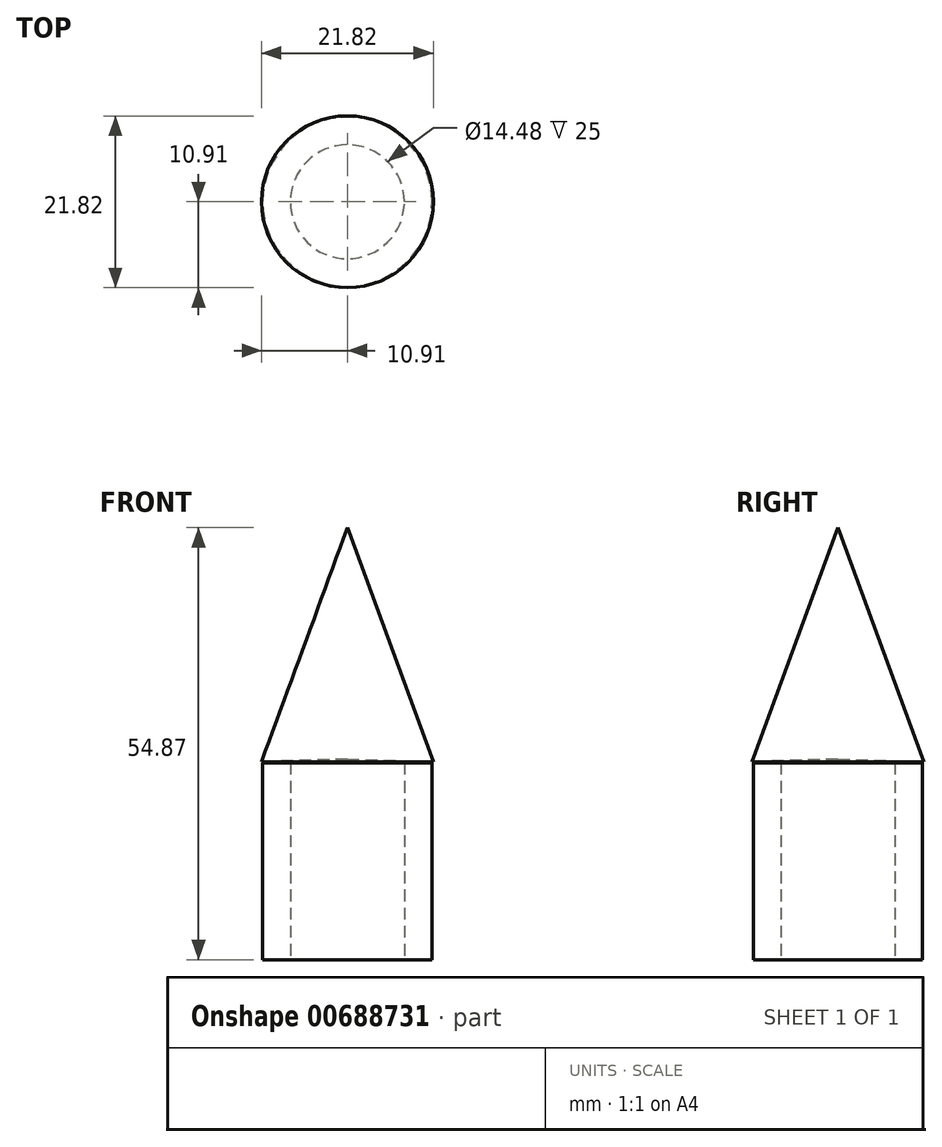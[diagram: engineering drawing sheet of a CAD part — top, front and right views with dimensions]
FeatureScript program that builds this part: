
annotation { "Feature Type Name" : "Feature", "Feature Type Description" : "" }
export const myFeature = defineFeature(function(context is Context, id is Id, definition is map)
    precondition{}
    {
        {
            var Q0;
            Q0=qCreatedBy(makeId("Top.planeOp"),FACE);
            var sketch = newSketch(context, id + "F0", { "sketchPlane" : qUnion([Q0])});
            skCircle(sketch, "E0", {"center": v(0, 0) * mm, "radius": 10.75 * mm});
            skCircle(sketch, "E1", {"center": v(0, 0) * mm, "radius": 7.24 * mm});
            skSolve(sketch);
        }
        {
            var Q0;
            Q0=makeQuery(id+"F0.imprint","IMPRINT",FACE,{"disambiguationData":[TD([[makeQuery(id+"F0.imprint","IMPRINT",EDGE,{"derivedFrom":sQuery(id+"F0.wireOp",EDGE,"E0")}),1.0]])]});
            extrude(context, id + "F1", {"entities" : qUnion([Q0]), "depth" : 25 * mm, "offsetDistance" : 25 * mm});
        }
        {
            var Q0;
            Q0=qCreatedBy(makeId("Right.planeOp"),FACE);
            var sketch = newSketch(context, id + "F2", { "sketchPlane" : qUnion([Q0])});
            skLineSegment(sketch, "E2", {"start": v(0, 25.46) * mm, "end": v(0, 54.87) * mm});
            skLineSegment(sketch, "E3", {"start": v(0, 54.87) * mm, "end": v(-10.91, 25.14) * mm});
            skLineSegment(sketch, "E4", {"start": v(-10.91, 25.14) * mm, "end": v(0, 25.46) * mm});
            skSolve(sketch);
        }
        {
            var Q0;
            Q0=qCreatedBy(makeId("Right.planeOp"),FACE);
            var sketch = newSketch(context, id + "F3", { "sketchPlane" : qUnion([Q0])});
            skLineSegment(sketch, "E5", {"start": v(0, 0) * mm, "end": v(0, 23.25) * mm});
            skSolve(sketch);
        }
        {
            var Q0;
            Q0=makeQuery(id+"F2.imprint","IMPRINT",FACE,{"disambiguationData":[TD([[makeQuery(id+"F2.imprint","IMPRINT",EDGE,{"derivedFrom":sQuery(id+"F2.wireOp",EDGE,"E2")}),1.0]])]});
            var Q1;
            Q1=sQuery(id+"F3.wireOp",EDGE,"E5");
            revolve(context, id + "F4", {"entities" : qUnion([Q0]), "axis" : qUnion([Q1]), "revolveType" : RevolveType.FULL});
        }
    });
